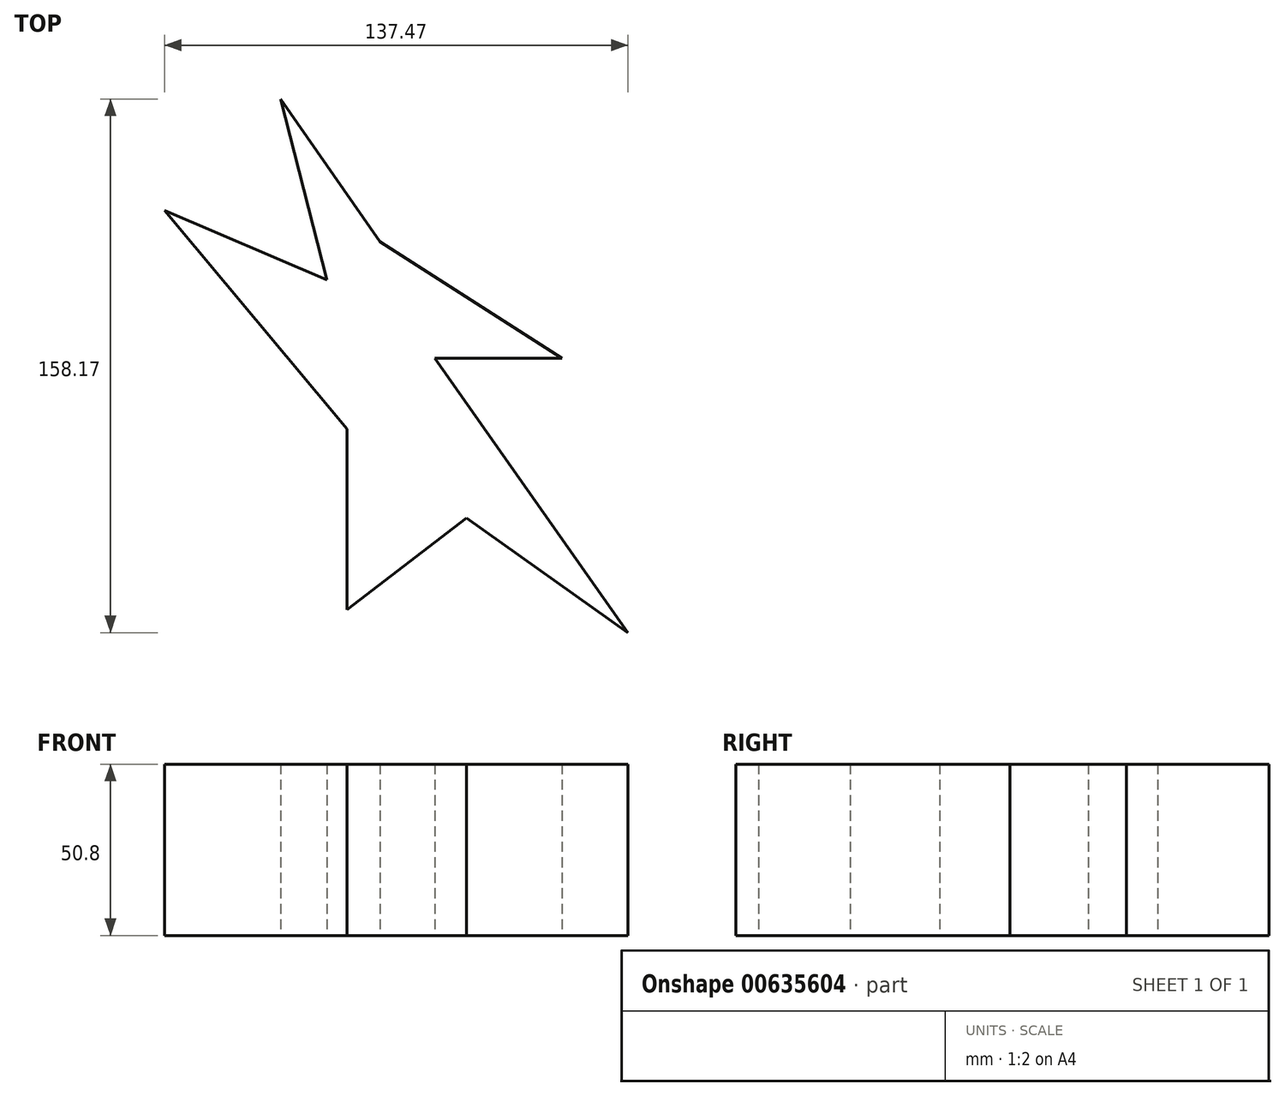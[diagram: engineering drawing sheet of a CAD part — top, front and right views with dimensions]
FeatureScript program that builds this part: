
annotation { "Feature Type Name" : "Feature", "Feature Type Description" : "" }
export const myFeature = defineFeature(function(context is Context, id is Id, definition is map)
    precondition{}
    {
        {
            var Q0;
            Q0=qCreatedBy(makeId("Top.planeOp"),FACE);
            var sketch = newSketch(context, id + "F0", { "sketchPlane" : qUnion([Q0])});
            skLineSegment(sketch, "E0", {"start": v(0, 0) * mm, "end": v(-28.2, 63.7) * mm});
            skLineSegment(sketch, "E1", {"start": v(-28.2, 63.7) * mm, "end": v(19.62, 29.75) * mm});
            skLineSegment(sketch, "E2", {"start": v(19.62, 29.75) * mm, "end": v(-37.59, 111.06) * mm});
            skLineSegment(sketch, "E3", {"start": v(-37.59, 111.06) * mm, "end": v(0, 111.06) * mm});
            skLineSegment(sketch, "E4", {"start": v(0, 111.06) * mm, "end": v(-53.88, 145.62) * mm});
            skLineSegment(sketch, "E5", {"start": v(-53.88, 145.62) * mm, "end": v(-83.43, 187.92) * mm});
            skLineSegment(sketch, "E6", {"start": v(-83.43, 187.92) * mm, "end": v(-69.7, 134.3) * mm});
            skLineSegment(sketch, "E7", {"start": v(-69.7, 134.3) * mm, "end": v(-117.85, 154.86) * mm});
            skLineSegment(sketch, "E8", {"start": v(-117.85, 154.86) * mm, "end": v(-63.63, 90.16) * mm});
            skLineSegment(sketch, "E9", {"start": v(-63.63, 90.16) * mm, "end": v(-63.63, 36.55) * mm});
            skLineSegment(sketch, "E10", {"start": v(-63.63, 36.55) * mm, "end": v(-28.2, 63.7) * mm});
            skLineSegment(sketch, "E11", {"start": v(-29.2, 99.14) * mm, "end": v(-18.14, 83.42) * mm});
            skSolve(sketch);
        }
        {
            var Q0;
            {var subQ0=sQuery(id+"F0.wireOp",EDGE,"E1");Q0=makeQuery(id+"F0.imprint","IMPRINT",FACE,{"disambiguationData":[TD([[makeQuery(id+"F0.imprint","IMPRINT",EDGE,{"derivedFrom":subQ0}),1.0]])]});}
            extrude(context, id + "F1", {"entities" : qUnion([Q0]), "depth" : 50.8 * mm, "offsetDistance" : 25.4 * mm});
        }
    });
